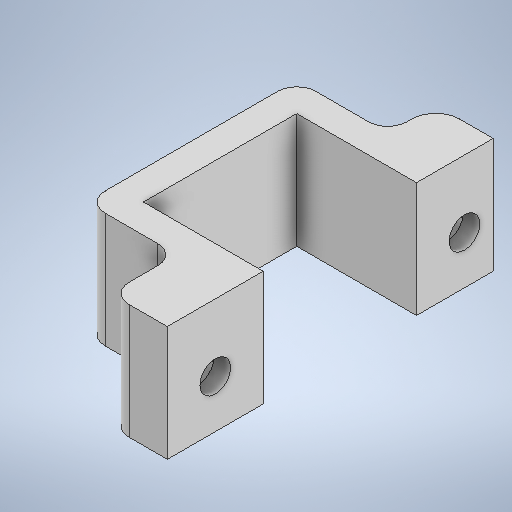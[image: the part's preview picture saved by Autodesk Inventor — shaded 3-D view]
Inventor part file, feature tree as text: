
AUTODESK INVENTOR PART (.ipt)
format: ipt  version: 2025.1 (Build 291241020, 241B)  size: 415,744 bytes
history: native  units: mm
features: extrude x7, sketch x6, plane x4, fillet x2, mirror x1, split x1, move_body x1, boolean_combine x1
ambient origin geometry x8: Origin, YZ Plane, XZ Plane, XY Plane, X Axis, Y Axis, Z Axis, Center Point
bodies: Solid1 (feature_tree), Solid2 (feature_tree), Solid3 (feature_tree)
feature tree (23):
  extrude  "Extrusion1"  Depth=16.0mm
  plane  "Work Plane1"
  sketch  "Sketch2"  dims[d3=22.0mm d4=3.0mm]
  extrude  "Extrusion2"  Depth=3.0mm
  extrude  "Extrusion3"  Depth=10.0mm
  plane  "Work Plane2"
  mirror  "Mirror1"
  extrude  "Extrusion4"  Depth=6.0mm
  plane  "Work Plane4"
  split  "Split1"
  move_body  "Move Body1"
  extrude  "Extrusion5"  [1 undecoded]
  boolean_combine  "Combine1"
  fillet  "Fillet3"  Radius=3.2mm
  extrude  "Extrusion6"  Depth=2.5mm
  extrude  "Extrusion7"  Depth=2.5mm TaperAngle=0.0deg
  fillet  "Fillet4"  Radius=0.75mm
  sketch  "Sketch1"  dims[d0=10.5mm d1=16.0mm]
  plane  "Work Plane3"
  sketch  "Sketch3"  dims[d5=10.0mm d6=10.0mm]
  sketch  "Sketch4"  dims[d7=6.0mm d8=6.0mm]
  sketch  "Sketch5"  dims[d9=14.0mm d10=0.0mm d11=-2.5mm d12=3.2mm]
  sketch  "Sketch6"  dims[d13=2.85mm d14=2.85mm d15=15.0mm d16=0.0mm d17=0.75mm d18=0.0mm d19=3.8mm d20=0.0mm d22=0.75mm d23=0.0mm d24=5.7mm d26=1.75mm d27=0.0mm d28=1.75mm d29=0.0mm d30=10.5mm d31=0.0mm d32=2.0mm d33=0.0mm d34=0.0mm d35=10.0mm d36=0.0mm d37=2.0mm d38=18.0mm d39=0.0mm d40=2.0mm d41=18.0mm d42=0.0mm d43=2.5mm d44=0.0mm d45=0.0mm d46=0.0mm]
note: 1 required parameter value undecoded (feature->parameter linkage not recoverable at this tier; creation-order binding heuristic only, values carry confidence <= 0.55)
